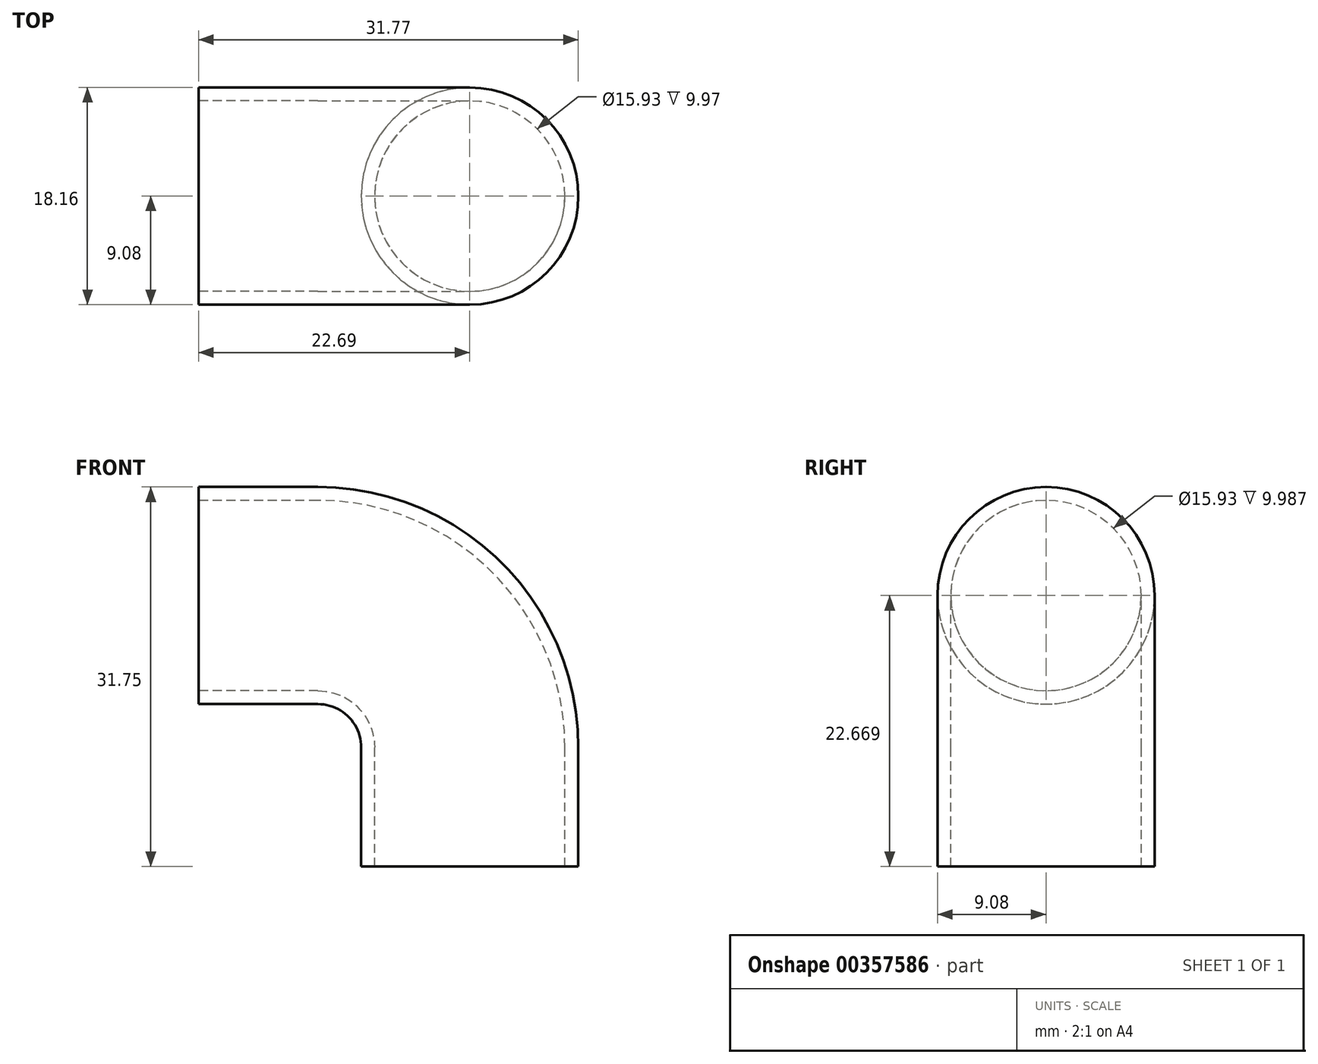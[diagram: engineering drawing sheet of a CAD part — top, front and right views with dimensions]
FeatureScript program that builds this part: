
annotation { "Feature Type Name" : "Feature", "Feature Type Description" : "" }
export const myFeature = defineFeature(function(context is Context, id is Id, definition is map)
    precondition{}
    {
        {
            var Q0;
            Q0=qCreatedBy(makeId("Top.planeOp"),FACE);
            var sketch = newSketch(context, id + "F0", { "sketchPlane" : qUnion([Q0])});
            skCircle(sketch, "E0", {"center": v(0, 0) * mm, "radius": 9.08 * mm});
            skCircle(sketch, "E1", {"center": v(0, 0) * mm, "radius": 7.96 * mm});
            skSolve(sketch);
        }
        {
            var Q0;
            Q0=qCreatedBy(makeId("Top.planeOp"),FACE);
            cPlane(context, id + "F1", {"entities" : qUnion([Q0]), "cplaneType" : CPlaneType.OFFSET, "offset" : 25.4 * mm, "width" : 152.4 * mm, "height" : 152.4 * mm});
        }
        {
            var Q0;
            Q0=qCreatedBy(makeId("Front.planeOp"),FACE);
            var sketch = newSketch(context, id + "F2", { "sketchPlane" : qUnion([Q0])});
            skLineSegment(sketch, "E2", {"start": v(0, 0) * mm, "end": v(0, 9.97) * mm});
            skLineSegment(sketch, "E3", {"start": v(-12.7, 22.67) * mm, "end": v(-22.69, 22.67) * mm});
            skPoint(sketch, "E4.visualSharp", {"position": v(0, 22.67) * mm});
            skArc(sketch, "E4.filletArc", {"start": v(0, 9.97) * mm, "mid": v(-3.72, 18.95) * mm, "end": v(-12.7, 22.67) * mm});
            skLineSegment(sketch, "E5", {"start": v(-22.69, 13.1) * mm, "end": v(-22.69, 33.38) * mm, "construction": true});
            skSolve(sketch);
        }
        {
            var Q0;
            Q0=makeQuery(id+"F0.imprint","IMPRINT",FACE,{"disambiguationData":[TD([[makeQuery(id+"F0.imprint","IMPRINT",EDGE,{"derivedFrom":sQuery(id+"F0.wireOp",EDGE,"E0")}),1.0]])]});
            var Q1;
            Q1=sQuery(id+"F2.wireOp",EDGE,"E2");
            var Q2;
            Q2=sQuery(id+"F2.wireOp",EDGE,"E4.filletArc");
            var Q3;
            Q3=sQuery(id+"F2.wireOp",EDGE,"E3");
            sweep(context, id + "F3", {"profiles" : qUnion([Q0]), "path" : qUnion([Q1, Q2, Q3])});
        }
    });
